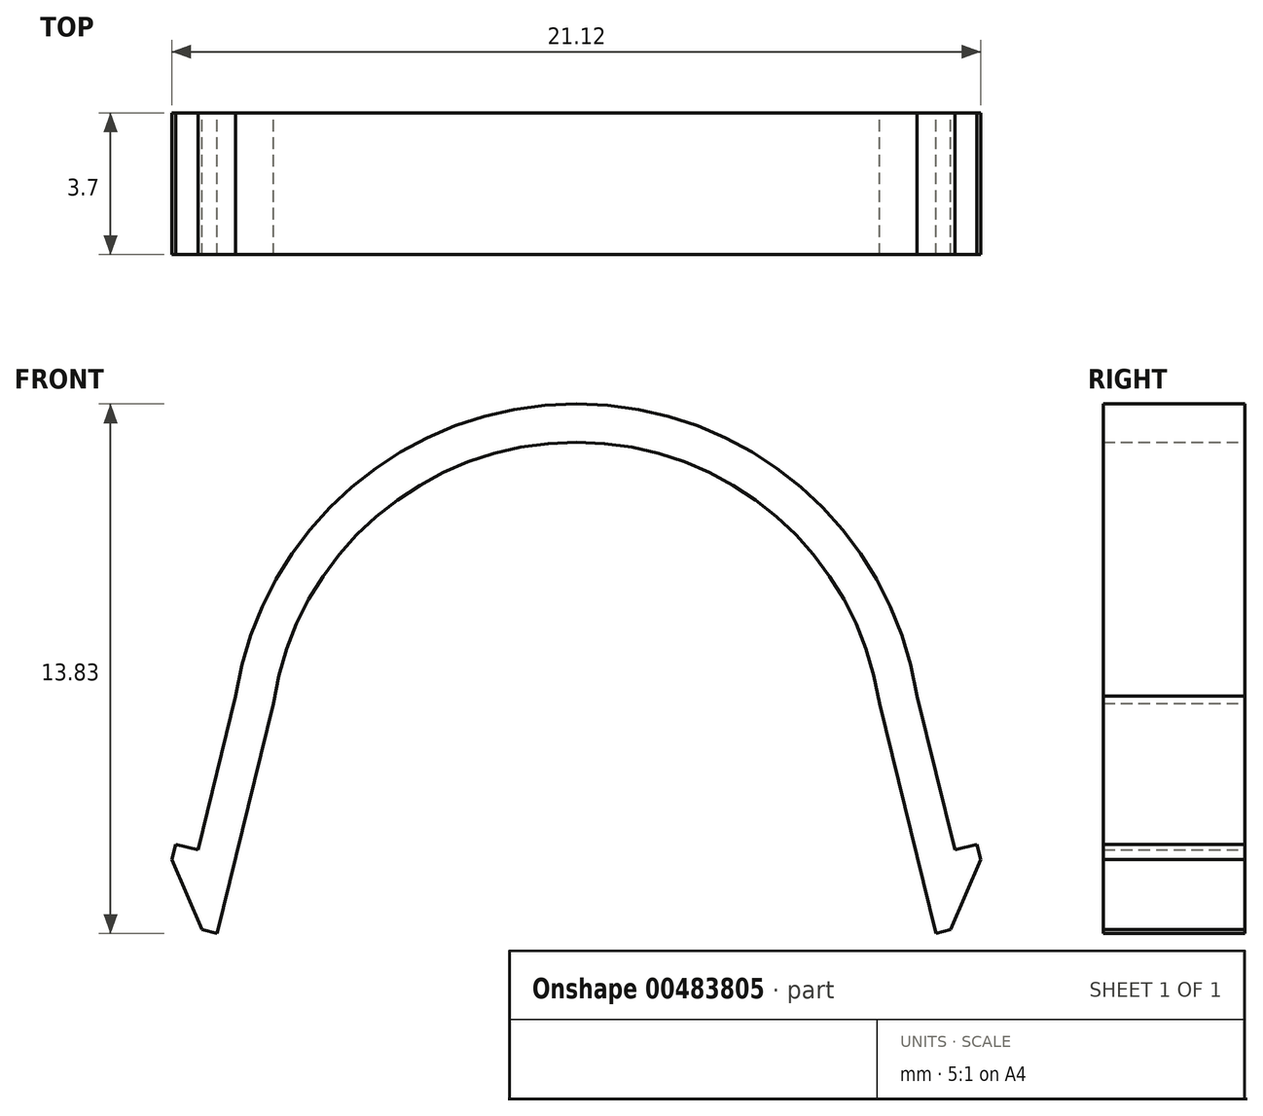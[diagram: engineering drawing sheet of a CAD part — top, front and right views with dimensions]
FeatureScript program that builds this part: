
annotation { "Feature Type Name" : "Feature", "Feature Type Description" : "" }
export const myFeature = defineFeature(function(context is Context, id is Id, definition is map)
    precondition{}
    {
        {
            var Q0;
            Q0=qCreatedBy(makeId("Front.planeOp"),FACE);
            var sketch = newSketch(context, id + "F0", { "sketchPlane" : qUnion([Q0])});
            skLineSegment(sketch, "E0", {"start": v(-9, 0) * mm, "end": v(-9, 2.6) * mm, "construction": true});
            skArc(sketch, "E1", {"start": v(0, 11.6) * mm, "mid": v(-6.36, 8.96) * mm, "end": v(-9, 2.6) * mm});
            skLineSegment(sketch, "E2", {"start": v(0, 38.36) * mm, "end": v(0, -11) * mm, "construction": true});
            skArc(sketch, "E3.0", {"start": v(0, 10.6) * mm, "mid": v(-5.66, 8.26) * mm, "end": v(-8, 2.6) * mm});
            skLineSegment(sketch, "E3.1", {"start": v(-8, -0.41) * mm, "end": v(-8, 2.6) * mm, "construction": true});
            skLineSegment(sketch, "E4", {"start": v(0, 11.6) * mm, "end": v(0, 10.6) * mm});
            skLineSegment(sketch, "E5", {"start": v(-9, 0) * mm, "end": v(-9.6, 0) * mm});
            skLineSegment(sketch, "E6", {"start": v(-9.6, 0) * mm, "end": v(-9.6, -0.5) * mm});
            skLineSegment(sketch, "E7", {"start": v(-9.6, -0.5) * mm, "end": v(-8.5, -1.8) * mm});
            skLineSegment(sketch, "E8", {"start": v(-8.5, -1.8) * mm, "end": v(-8, -1.8) * mm});
            skLineSegment(sketch, "E9", {"start": v(-8, -1.8) * mm, "end": v(-8, -0.41) * mm});
            skLineSegment(sketch, "E10", {"start": v(-8.9, 3.98) * mm, "end": v(-9.88, -0.05) * mm});
            skLineSegment(sketch, "E11.0", {"start": v(-7.91, 3.78) * mm, "end": v(-9.38, -2.23) * mm});
            skLineSegment(sketch, "E12", {"start": v(-10.46, 0.1) * mm, "end": v(-9.88, -0.05) * mm});
            skLineSegment(sketch, "E13", {"start": v(-10.46, 0.1) * mm, "end": v(-10.56, -0.3) * mm});
            skLineSegment(sketch, "E14", {"start": v(-10.56, -0.3) * mm, "end": v(-9.77, -2.13) * mm});
            skLineSegment(sketch, "E15", {"start": v(-9.77, -2.13) * mm, "end": v(-9.38, -2.23) * mm});
            skLineSegment(sketch, "E16.MirrorCS", {"start": v(8.5, -1.8) * mm, "end": v(8, -1.8) * mm});
            skLineSegment(sketch, "E17.MirrorCS", {"start": v(10.46, 0.1) * mm, "end": v(9.88, -0.05) * mm});
            skLineSegment(sketch, "E18.MirrorCS", {"start": v(10.46, 0.1) * mm, "end": v(10.56, -0.3) * mm});
            skLineSegment(sketch, "E19.MirrorCS", {"start": v(9, 0) * mm, "end": v(9.6, 0) * mm});
            skLineSegment(sketch, "E20.MirrorCS", {"start": v(9.6, 0) * mm, "end": v(9.6, -0.5) * mm});
            skLineSegment(sketch, "E21.MirrorCS", {"start": v(9.77, -2.13) * mm, "end": v(9.38, -2.23) * mm});
            skArc(sketch, "E22.MirrorCS", {"start": v(0, 11.6) * mm, "mid": v(6.36, 8.96) * mm, "end": v(9, 2.6) * mm});
            skLineSegment(sketch, "E23.MirrorCS", {"start": v(7.91, 3.78) * mm, "end": v(9.38, -2.23) * mm});
            skArc(sketch, "E24.MirrorCS", {"start": v(0, 10.6) * mm, "mid": v(5.66, 8.26) * mm, "end": v(8, 2.6) * mm});
            skLineSegment(sketch, "E25.MirrorCS", {"start": v(10.56, -0.3) * mm, "end": v(9.77, -2.13) * mm});
            skLineSegment(sketch, "E26.MirrorCS", {"start": v(8.9, 3.98) * mm, "end": v(9.88, -0.05) * mm});
            skLineSegment(sketch, "E27.MirrorCS", {"start": v(9.6, -0.5) * mm, "end": v(8.5, -1.8) * mm});
            skLineSegment(sketch, "E28.MirrorCS", {"start": v(9, 0) * mm, "end": v(9, 2.6) * mm, "construction": true});
            skLineSegment(sketch, "E29.MirrorCS", {"start": v(8, -0.41) * mm, "end": v(8, 2.6) * mm, "construction": true});
            skLineSegment(sketch, "E30.MirrorCS", {"start": v(8, -1.8) * mm, "end": v(8, -0.41) * mm});
            skSolve(sketch);
        }
        {
            var Q0;
            Q0=qSketchRegion(id+"F0",true);
            extrude(context, id + "F1", {"entities" : qUnion([Q0]), "depth" : 3.7 * mm});
        }
    });
